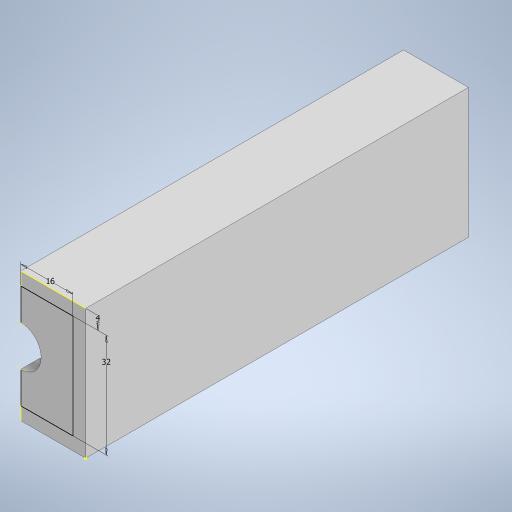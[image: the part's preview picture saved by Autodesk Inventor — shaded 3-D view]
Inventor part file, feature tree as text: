
AUTODESK INVENTOR PART (.ipt)
format: ipt  version: 2023 (Build 270158000, 158)  size: 241,152 bytes
history: native  units: in
note: dims shown in document units (in); Inventor stores cm internally (conversion verified against a paired STEP export)
features: sketch x7, extrude x3, other x1
ambient origin geometry x8: Origin, YZ Plane, XZ Plane, XY Plane, X Axis, Y Axis, Z Axis, Center Point
bodies: Body1 (feature_tree)
feature tree (11):
  other  "솔리드1"
  extrude  "돌출1"  Depth=1.5748in
  sketch  "스케치2"
  sketch  "스케치3"
  sketch  "스케치4"
  sketch  "스케치5"
  extrude  "돌출2"  Depth=0.7874in
  extrude  "돌출4"  Depth=0.7874in
  sketch  "스케치1"
  sketch  "스케치6"
  sketch  "스케치8"
